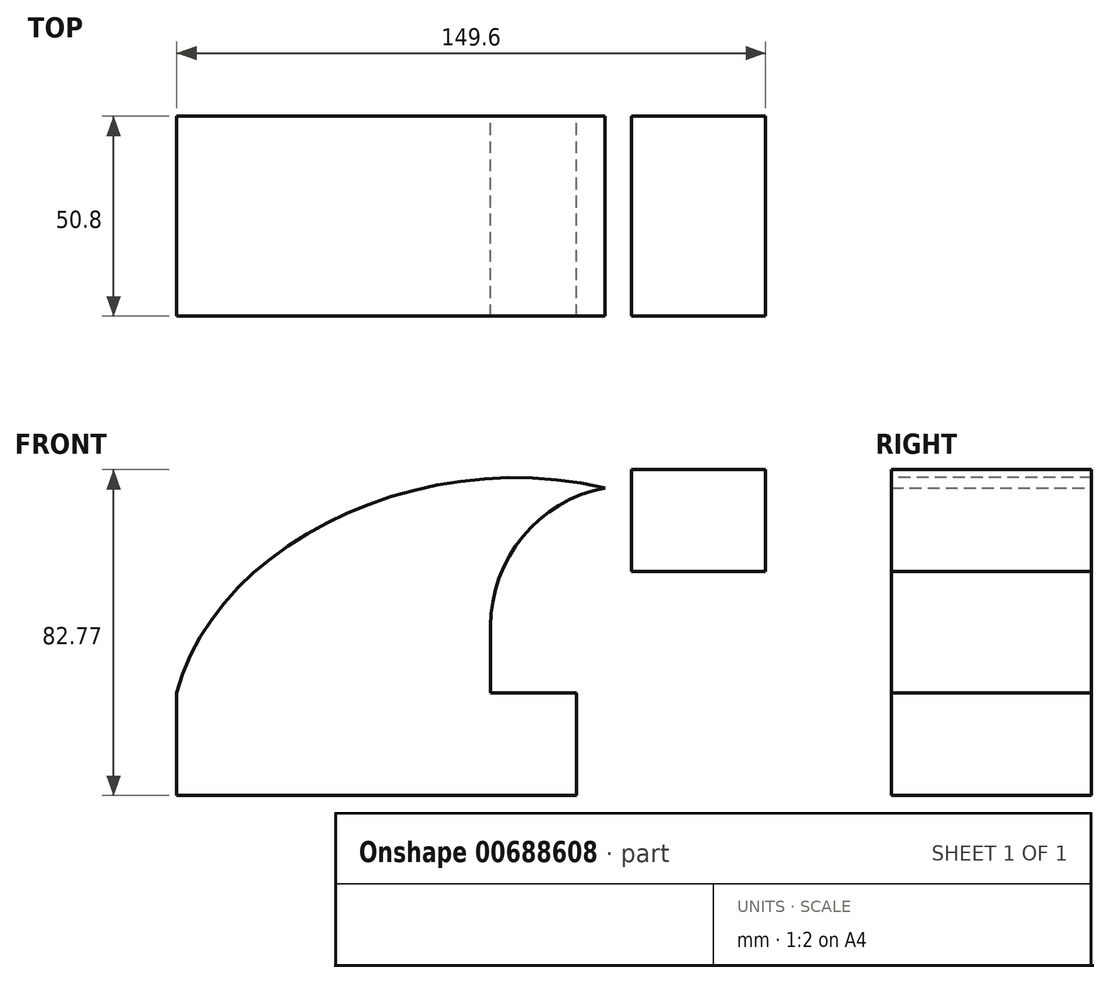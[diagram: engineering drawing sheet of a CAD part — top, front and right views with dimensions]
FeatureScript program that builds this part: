
annotation { "Feature Type Name" : "Feature", "Feature Type Description" : "" }
export const myFeature = defineFeature(function(context is Context, id is Id, definition is map)
    precondition{}
    {
        {
            var Q0;
            Q0=qCreatedBy(makeId("Front.planeOp"),FACE);
            var sketch = newSketch(context, id + "F0", { "sketchPlane" : qUnion([Q0])});
            skLineSegment(sketch, "E0.bottom", {"start": v(50.8, -13) * mm, "end": v(-50.8, -13) * mm});
            skLineSegment(sketch, "E0.top", {"start": v(50.8, 13) * mm, "end": v(-50.8, 13) * mm});
            skLineSegment(sketch, "E0.left", {"start": v(50.8, -13) * mm, "end": v(50.8, 13) * mm});
            skLineSegment(sketch, "E0.right", {"start": v(-50.8, -13) * mm, "end": v(-50.8, 13) * mm});
            skPoint(sketch, "E0.middle", {"position": v(0, 0) * mm});
            skLineSegment(sketch, "E1.bottom", {"start": v(98.8, 43.93) * mm, "end": v(64.7, 43.93) * mm});
            skLineSegment(sketch, "E1.top", {"start": v(98.8, 69.78) * mm, "end": v(64.7, 69.78) * mm});
            skLineSegment(sketch, "E1.left", {"start": v(98.8, 43.93) * mm, "end": v(98.8, 69.78) * mm});
            skLineSegment(sketch, "E1.right", {"start": v(64.7, 43.93) * mm, "end": v(64.7, 69.78) * mm});
            skPoint(sketch, "E1.middle", {"position": v(81.75, 56.86) * mm});
            skLineSegment(sketch, "E2", {"start": v(50.8, 13) * mm, "end": v(50.8, 30.03) * mm});
            skArc(sketch, "E3", {"start": v(64.7, 43.93) * mm, "mid": v(54.87, 39.86) * mm, "end": v(50.8, 30.03) * mm});
            skArc(sketch, "E4.0", {"start": v(64.66, 65.78) * mm, "mid": v(39.41, 55.3) * mm, "end": v(28.96, 30.03) * mm});
            skLineSegment(sketch, "E5", {"start": v(28.96, 30.03) * mm, "end": v(28.96, 13) * mm});
            skFitSpline(sketch, "E6", {"points": [v(-50.8, 13) * mm, v(57.98, 65.14) * mm], "startDerivative": vector(30.07, 114.95) * mm, "endDerivative": vector(139.09, -32.77) * mm});
            skSolve(sketch);
        }
        {
            var Q0;
            Q0 = qSketchRegion(id + "F0", true);
            extrude(context, id + "F1", {"entities" : qUnion([Q0]), "endBound" : BoundingType.SYMMETRIC, "depth" : 50.8 * mm, "offsetDistance" : 25.4 * mm});
        }
    });
